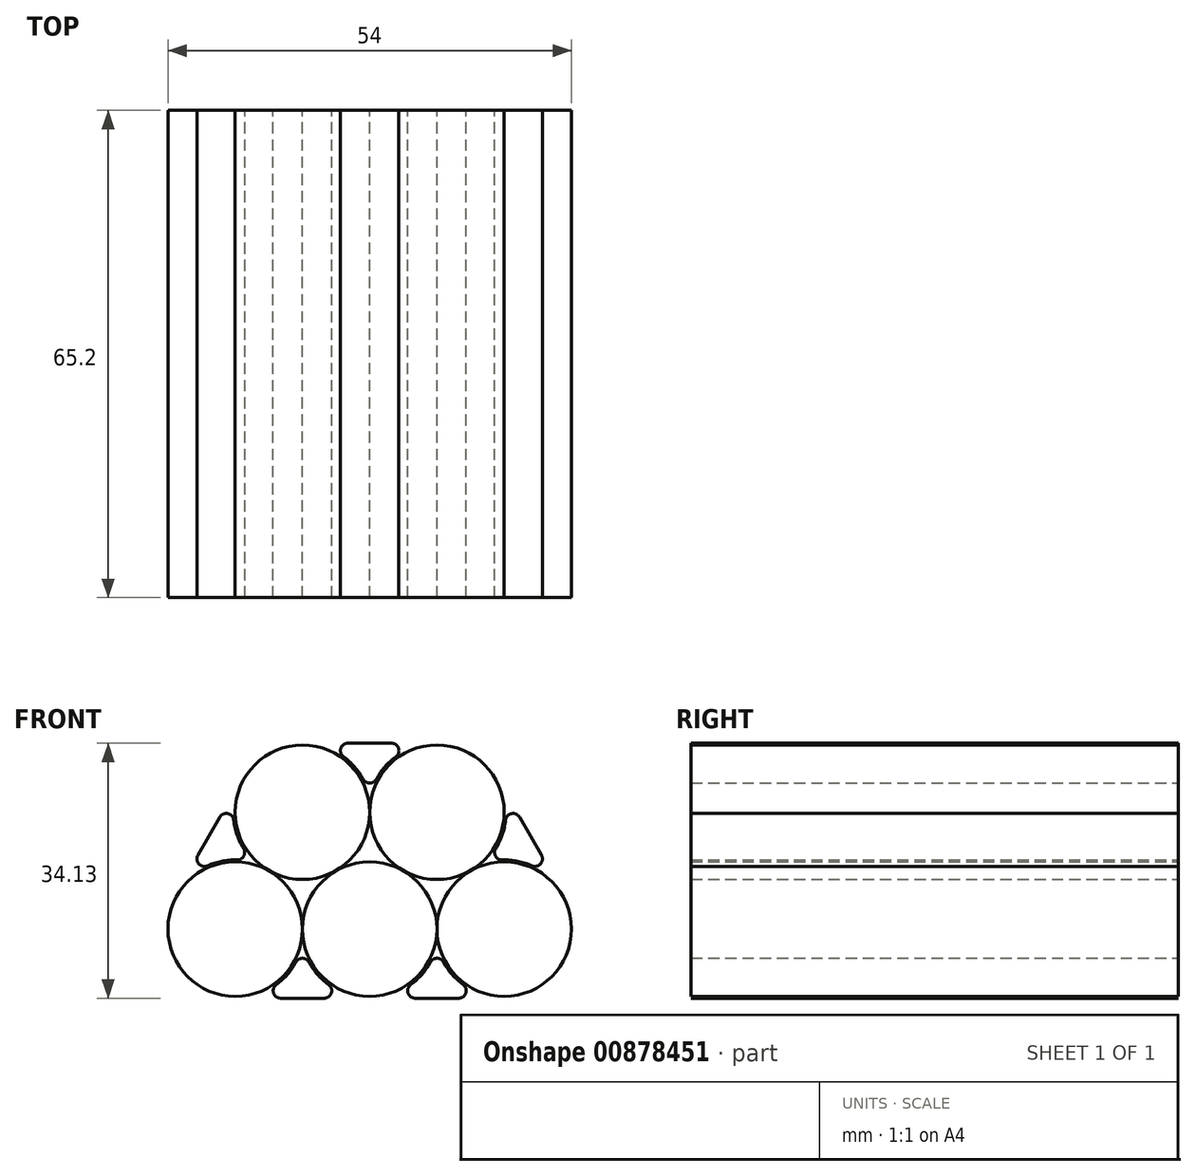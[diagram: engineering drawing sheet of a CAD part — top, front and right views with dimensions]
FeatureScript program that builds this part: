
annotation { "Feature Type Name" : "Feature", "Feature Type Description" : "" }
export const myFeature = defineFeature(function(context is Context, id is Id, definition is map)
    precondition{}
    {
        {
            var Q0;
            Q0=qCreatedBy(makeId("Front.planeOp"),FACE);
            var sketch = newSketch(context, id + "F0", { "sketchPlane" : qUnion([Q0])});
            skCircle(sketch, "E0", {"center": v(-18, 0) * mm, "radius": 9 * mm});
            skCircle(sketch, "E1.1.0.0", {"center": v(0, 0) * mm, "radius": 9 * mm});
            skCircle(sketch, "E1.2.0.0", {"center": v(18, 0) * mm, "radius": 9 * mm});
            skLineSegment(sketch, "E1.direction1", {"start": v(-18, 0) * mm, "end": v(0, 0) * mm, "construction": true});
            skCircle(sketch, "E2", {"center": v(-9, 15.63) * mm, "radius": 9 * mm});
            skCircle(sketch, "E3.1.0.0", {"center": v(9, 15.63) * mm, "radius": 9 * mm});
            skLineSegment(sketch, "E3.direction1", {"start": v(-9, 15.63) * mm, "end": v(9, 15.63) * mm, "construction": true});
            skSolve(sketch);
        }
        {
            var Q0;
            Q0 = qSketchRegion(id + "F0", true);
            extrude(context, id + "F1", {"entities" : qUnion([Q0]), "depth" : 65.2 * mm, "offsetDistance" : 25 * mm});
        }
        {
            var Q0;
            Q0=qCreatedBy(makeId("Front.planeOp"),FACE);
            var sketch = newSketch(context, id + "F2", { "sketchPlane" : qUnion([Q0])});
            skLineSegment(sketch, "E4", {"start": v(27.25, -9.25) * mm, "end": v(27.25, 24.88) * mm, "construction": true});
            skLineSegment(sketch, "E5", {"start": v(-27.25, 24.88) * mm, "end": v(-27.25, -9.25) * mm, "construction": true});
            skLineSegment(sketch, "E6", {"start": v(22.98, 9.89) * mm, "end": v(20.05, 14.98) * mm});
            skLineSegment(sketch, "E7", {"start": v(2.91, 24.88) * mm, "end": v(-2.92, 24.88) * mm});
            skLineSegment(sketch, "E8", {"start": v(-20.05, 14.98) * mm, "end": v(-22.98, 9.89) * mm});
            skLineSegment(sketch, "E9", {"start": v(-11.92, -9.25) * mm, "end": v(-6.08, -9.25) * mm});
            skArc(sketch, "E10", {"start": v(21.71, 8.47) * mm, "mid": v(19.77, 9.08) * mm, "end": v(17.75, 9.25) * mm});
            skArc(sketch, "E11", {"start": v(9.88, -4.43) * mm, "mid": v(11.03, -6.08) * mm, "end": v(12.51, -7.45) * mm});
            skArc(sketch, "E12", {"start": v(-8.12, -4.43) * mm, "mid": v(-6.97, -6.08) * mm, "end": v(-5.49, -7.45) * mm});
            skArc(sketch, "E13", {"start": v(-17.75, 9.25) * mm, "mid": v(-19.78, 9.08) * mm, "end": v(-21.71, 8.47) * mm});
            skArc(sketch, "E14", {"start": v(16.87, 10.77) * mm, "mid": v(17.74, 12.6) * mm, "end": v(18.19, 14.6) * mm});
            skArc(sketch, "E15", {"start": v(-0.88, 20.06) * mm, "mid": v(-2.03, 21.71) * mm, "end": v(-3.51, 23.08) * mm});
            skArc(sketch, "E16", {"start": v(-12.51, -7.45) * mm, "mid": v(-11.03, -6.08) * mm, "end": v(-9.88, -4.43) * mm});
            skArc(sketch, "E17", {"start": v(3.5, 23.08) * mm, "mid": v(2.03, 21.71) * mm, "end": v(0.88, 20.06) * mm});
            skArc(sketch, "E18", {"start": v(-18.2, 14.59) * mm, "mid": v(-17.74, 12.6) * mm, "end": v(-16.87, 10.77) * mm});
            skPoint(sketch, "E19.visualSharp", {"position": v(17.01, 20.25) * mm});
            skArc(sketch, "E19.filletArc", {"start": v(20.05, 14.98) * mm, "mid": v(18.98, 15.46) * mm, "end": v(18.19, 14.6) * mm});
            skPoint(sketch, "E20.visualSharp", {"position": v(26.02, 4.62) * mm});
            skArc(sketch, "E20.filletArc", {"start": v(21.71, 8.47) * mm, "mid": v(22.86, 8.72) * mm, "end": v(22.98, 9.89) * mm});
            skPoint(sketch, "E21.visualSharp", {"position": v(15.28, 8.84) * mm});
            skArc(sketch, "E21.filletArc", {"start": v(16.87, 10.77) * mm, "mid": v(16.85, 9.75) * mm, "end": v(17.75, 9.25) * mm});
            skPoint(sketch, "E22.visualSharp", {"position": v(-15.28, 8.84) * mm});
            skArc(sketch, "E22.filletArc", {"start": v(-17.75, 9.25) * mm, "mid": v(-16.86, 9.75) * mm, "end": v(-16.87, 10.77) * mm});
            skPoint(sketch, "E23.visualSharp", {"position": v(-26.02, 4.61) * mm});
            skArc(sketch, "E23.filletArc", {"start": v(-22.98, 9.89) * mm, "mid": v(-22.86, 8.72) * mm, "end": v(-21.71, 8.47) * mm});
            skPoint(sketch, "E24.visualSharp", {"position": v(-17.02, 20.25) * mm});
            skArc(sketch, "E24.filletArc", {"start": v(-18.2, 14.59) * mm, "mid": v(-18.98, 15.46) * mm, "end": v(-20.05, 14.98) * mm});
            skPoint(sketch, "E25.visualSharp", {"position": v(9, 24.88) * mm});
            skArc(sketch, "E25.filletArc", {"start": v(3.5, 23.08) * mm, "mid": v(3.86, 24.2) * mm, "end": v(2.91, 24.88) * mm});
            skPoint(sketch, "E26.visualSharp", {"position": v(-9, 24.88) * mm});
            skArc(sketch, "E26.filletArc", {"start": v(-2.92, 24.88) * mm, "mid": v(-3.87, 24.2) * mm, "end": v(-3.51, 23.08) * mm});
            skPoint(sketch, "E27.visualSharp", {"position": v(0, 17.77) * mm});
            skArc(sketch, "E27.filletArc", {"start": v(-0.88, 20.06) * mm, "mid": v(0, 19.54) * mm, "end": v(0.88, 20.06) * mm});
            skLineSegment(sketch, "E28", {"start": v(6.08, -9.25) * mm, "end": v(11.92, -9.25) * mm});
            skArc(sketch, "E29", {"start": v(5.49, -7.45) * mm, "mid": v(6.97, -6.08) * mm, "end": v(8.12, -4.43) * mm});
            skPoint(sketch, "E30.visualSharp", {"position": v(0, -9.25) * mm});
            skArc(sketch, "E30.filletArc", {"start": v(-6.08, -9.25) * mm, "mid": v(-5.13, -8.56) * mm, "end": v(-5.49, -7.45) * mm});
            skArc(sketch, "E31.filletArc", {"start": v(5.49, -7.45) * mm, "mid": v(5.13, -8.56) * mm, "end": v(6.08, -9.25) * mm});
            skPoint(sketch, "E32.visualSharp", {"position": v(9, -2.14) * mm});
            skArc(sketch, "E32.filletArc", {"start": v(9.88, -4.43) * mm, "mid": v(9, -3.9) * mm, "end": v(8.12, -4.43) * mm});
            skPoint(sketch, "E33.visualSharp", {"position": v(18, -9.25) * mm});
            skArc(sketch, "E33.filletArc", {"start": v(11.92, -9.25) * mm, "mid": v(12.87, -8.56) * mm, "end": v(12.51, -7.45) * mm});
            skPoint(sketch, "E34.visualSharp", {"position": v(-9, -2.14) * mm});
            skArc(sketch, "E34.filletArc", {"start": v(-8.12, -4.43) * mm, "mid": v(-9, -3.9) * mm, "end": v(-9.88, -4.43) * mm});
            skPoint(sketch, "E35.visualSharp", {"position": v(-18, -9.25) * mm});
            skArc(sketch, "E35.filletArc", {"start": v(-12.51, -7.45) * mm, "mid": v(-12.87, -8.56) * mm, "end": v(-11.92, -9.25) * mm});
            skSolve(sketch);
        }
        {
            var Q0;
            Q0 = qSketchRegion(id + "F2", true);
            extrude(context, id + "F3", {"entities" : qUnion([Q0]), "depth" : 65.2 * mm, "offsetDistance" : 25 * mm});
        }
    });
